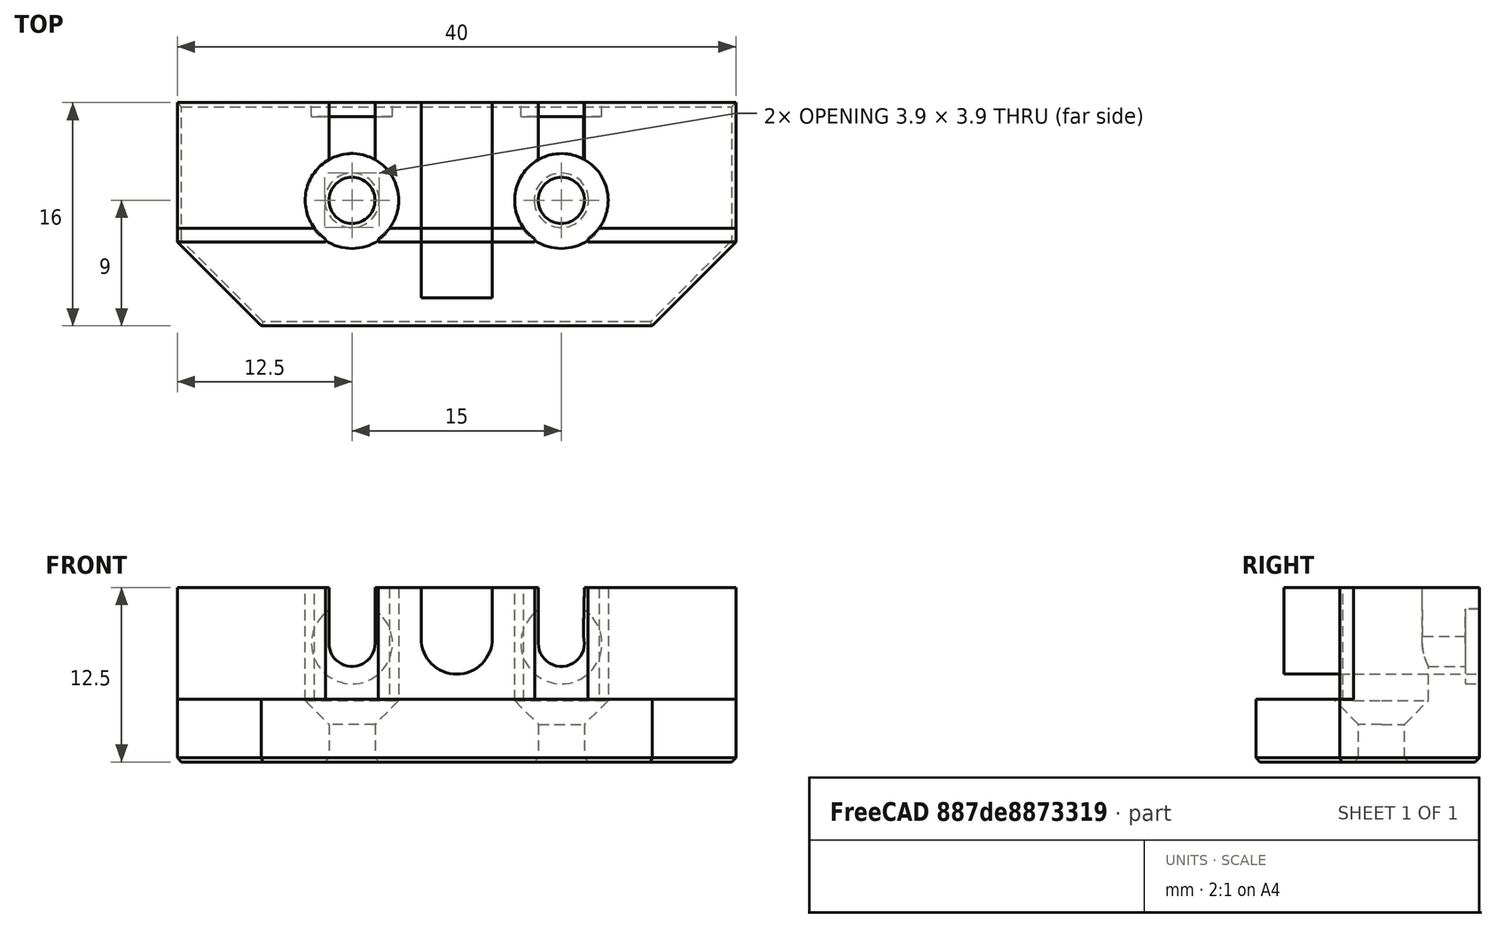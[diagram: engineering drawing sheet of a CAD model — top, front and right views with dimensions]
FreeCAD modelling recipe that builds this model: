
FCSTD DOCUMENT  (FreeCAD 0.15R4527 (Git))
Label: lower nozzle mount 1mm
License: All rights reserved
LicenseURL: http://en.wikipedia.org/wiki/All_rights_reserved
objects: Sketcher::SketchObject×2, Part::Feature×1, PartDesign::Pad×1, PartDesign::Pocket×1, Mesh::Feature×1
note: 7 computed .brp shape members not serialized (recipe doc carries the construction recipe); baked Part::Feature solids carry a one-line shape summary decoded from their .brp

FEATURE [Part::Feature] Part__Feature  label="nozzle-mount"
  shape: bbox 40 x 16 x 12.5 mm, 54 faces (baked)
FEATURE [Sketcher::SketchObject] Sketch
  ExternalGeometry = -> [Part__Feature]
  Placement = pos=(0,0,4.5) rot=(0,0,1;0rad)
  Support = -> Part__Feature [Face4]
  sketch-geometry (16):
    g0: LineSegment StartX=-20 StartY=7 StartZ=0 EndX=-20 EndY=6 EndZ=0
    g1: LineSegment StartX=20 StartY=7 StartZ=0 EndX=20 EndY=6 EndZ=0
    g2: LineSegment StartX=20 StartY=6 StartZ=0 EndX=9.4 EndY=6 EndZ=0
    g3: LineSegment StartX=5.6 StartY=6 StartZ=0 EndX=-5.6 EndY=6 EndZ=0
    g4: LineSegment StartX=-9.4 StartY=6 StartZ=0 EndX=-20 EndY=6 EndZ=0
    g5: LineSegment StartX=-20 StartY=7 StartZ=0 EndX=-10.1875 EndY=7 EndZ=0
    g6: LineSegment StartX=4.81253 StartY=7 StartZ=0 EndX=-4.81253 EndY=7 EndZ=0
    g7: LineSegment StartX=20 StartY=7 StartZ=0 EndX=10.1875 EndY=7 EndZ=0
    g8: ArcOfCircle CenterX=-7.5 CenterY=9 CenterZ=0 NormalX=0 NormalY=0 NormalZ=1 Radius=3.35 StartAngle=3.78137 EndAngle=4.10933
    g9: ArcOfCircle CenterX=-7.5 CenterY=9 CenterZ=0 NormalX=0 NormalY=0 NormalZ=1 Radius=3.35 StartAngle=5.31545 EndAngle=5.64341
    g10: ArcOfCircle CenterX=7.5 CenterY=9 CenterZ=0 NormalX=0 NormalY=0 NormalZ=1 Radius=3.35 StartAngle=3.78137 EndAngle=4.10933
    g11: ArcOfCircle CenterX=7.5 CenterY=9 CenterZ=0 NormalX=0 NormalY=0 NormalZ=1 Radius=3.35 StartAngle=5.31545 EndAngle=5.64341
    g12: LineSegment StartX=5.6 StartY=6.24092 StartZ=0 EndX=5.6 EndY=6 EndZ=0
    g13: LineSegment StartX=9.4 StartY=6.24092 StartZ=0 EndX=9.4 EndY=6 EndZ=0
    g14: LineSegment StartX=-5.6 StartY=6.24092 StartZ=0 EndX=-5.6 EndY=6 EndZ=0
    g15: LineSegment StartX=-9.4 StartY=6.24092 StartZ=0 EndX=-9.4 EndY=6 EndZ=0
  constraints (40):
    c: Coincident(g1,g-5)
    c: Coincident(g0,g4)
    c: Coincident(g-4,g0)
    c: Coincident(g5,g0)
    c: Coincident(g7,g1)
    c: Coincident(g1,g-6)
    c: Coincident(g1,g2)
    c: Coincident(g0,g-3)
    c: Coincident(g-9,g6)
    c: Coincident(g7,g-10)
    c: Coincident(g6,g-7)
    c: Coincident(g5,g-8)
    c: Coincident(g8,g-11)
    c: Coincident(g8,g5)
    c: Coincident(g9,g8)
    c: Coincident(g9,g6)
    c: Coincident(g10,g-12)
    c: Coincident(g10,g6)
    c: Coincident(g11,g10)
    c: Coincident(g11,g7)
    c: Vertical(g12)
    c: Vertical(g13)
    c: Vertical(g14)
    c: Vertical(g15)
    c: Coincident(g8,g15)
    c: Coincident(g4,g15)
    c: DistanceX(g8,g-16) = 0.25
    c: Coincident(g9,g14)
    c: Coincident(g3,g14)
    c: DistanceY(g3,g4) = 0
    c: Horizontal(g4)
    c: Horizontal(g3)
    c: DistanceX(g9,g-15) = -0.25
    c: Coincident(g10,g12)
    c: Coincident(g3,g12)
    c: Coincident(g11,g13)
    c: Coincident(g2,g13)
    c: Horizontal(g2)
    c: DistanceX(g-13,g10) = -0.25
    c: DistanceX(g11,g-14) = -0.25
FEATURE [PartDesign::Pad] Pad
  Length = 8
  Length2 = 2
  Midplane = true
  Sketch = -> Sketch
  Type = 4
  UpToFace = -> Part__Feature [Face18]
FEATURE [Sketcher::SketchObject] Sketch002
  ExternalGeometry = -> [Pad]
  Placement = pos=(0,7,0) rot=(0,0.707107,0.707107;3.14159rad)
  Support = -> Pad [Face37]
  sketch-geometry (4):
    g0: LineSegment StartX=-2.55 StartY=12.5 StartZ=0 EndX=2.55 EndY=12.5 EndZ=0
    g1: LineSegment StartX=-2.55 StartY=8.84613 StartZ=0 EndX=-2.55 EndY=12.5 EndZ=0
    g2: LineSegment StartX=2.55 StartY=12.5 StartZ=0 EndX=2.55 EndY=8.84613 EndZ=0
    g3: ArcOfCircle CenterX=0 CenterY=8.84613 CenterZ=0 NormalX=0 NormalY=0 NormalZ=1 Radius=2.55 StartAngle=3.14159 EndAngle=6.28319
  constraints (13):
    c: DistanceY(g1) = 8.84613
    c: DistanceX(g3) = 0
    c: DistanceY(g3) = 8.84613
    c: DistanceX(g0) = -2.55
    c: DistanceY(g0) = 12.5
    c: DistanceX(g0) = 2.55
    c: DistanceY(g0) = 12.5
    c: DistanceX(g2) = 2.55
    c: DistanceY(g2) = 8.84613
    c: Coincident(g3,g1)
    c: Coincident(g0,g1)
    c: Coincident(g0,g2)
    c: Coincident(g3,g2)
FEATURE [PartDesign::Pocket] Pocket
  Length = 5
  Sketch = -> Sketch002
  Type = 0
FEATURE [Mesh::Feature] Mesh001  label="Pocket (Meshed)001"
